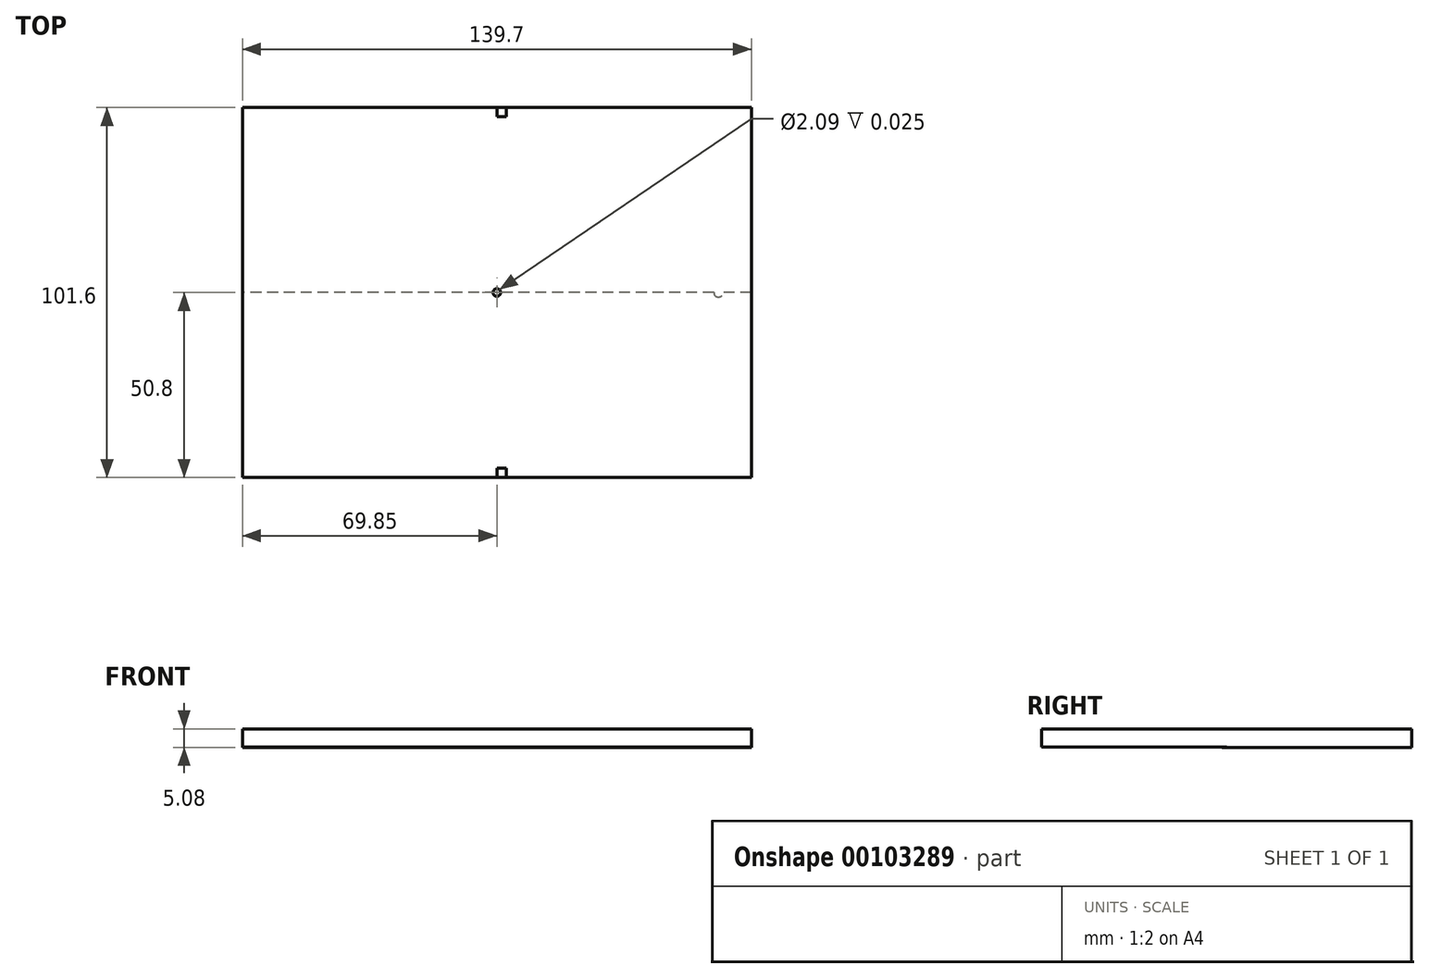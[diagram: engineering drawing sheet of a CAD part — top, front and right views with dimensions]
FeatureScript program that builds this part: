
annotation { "Feature Type Name" : "Feature", "Feature Type Description" : "" }
export const myFeature = defineFeature(function(context is Context, id is Id, definition is map)
    precondition{}
    {
        {
            var Q0;
            Q0=qCreatedBy(makeId("Top.planeOp"),FACE);
            var sketch = newSketch(context, id + "F0", { "sketchPlane" : qUnion([Q0])});
            skLineSegment(sketch, "E0.bottom", {"start": v(0, 0) * mm, "end": v(139.7, 0) * mm});
            skLineSegment(sketch, "E0.top", {"start": v(0, 101.6) * mm, "end": v(139.7, 101.6) * mm});
            skLineSegment(sketch, "E0.left", {"start": v(0, 0) * mm, "end": v(0, 101.6) * mm});
            skLineSegment(sketch, "E0.right", {"start": v(139.7, 0) * mm, "end": v(139.7, 101.6) * mm});
            skSolve(sketch);
        }
        {
            var Q0;
            Q0=makeQuery(id+"F0.imprint","IMPRINT",FACE,{"disambiguationData":[TD([[makeQuery(id+"F0.imprint","IMPRINT",EDGE,{"derivedFrom":sQuery(id+"F0.wireOp",EDGE,"E0.bottom")}),1.0]])]});
            extrude(context, id + "F1", {"entities" : qUnion([Q0]), "depth" : 5.08 * mm});
        }
        {
            var Q0;
            Q0=makeQuery(id+"F1.opExtrude","CAP_FACE",FACE,{"disambiguationData":[OSD([sQuery(id+"F0.wireOp",EDGE,"E0.bottom"),sQuery(id+"F0.wireOp",EDGE,"E0.top"),sQuery(id+"F0.wireOp",EDGE,"E0.left"),sQuery(id+"F0.wireOp",EDGE,"E0.right")])],"isStart":false});
            var sketch = newSketch(context, id + "F2", { "sketchPlane" : qUnion([Q0])});
            skLineSegment(sketch, "E1.bottom", {"start": v(69.85, 0) * mm, "end": v(72.4, 0) * mm});
            skLineSegment(sketch, "E1.top", {"start": v(69.85, 2.54) * mm, "end": v(72.4, 2.54) * mm});
            skLineSegment(sketch, "E1.left", {"start": v(69.85, 0) * mm, "end": v(69.85, 2.54) * mm});
            skLineSegment(sketch, "E1.right", {"start": v(72.4, 0) * mm, "end": v(72.4, 2.54) * mm});
            skLineSegment(sketch, "E2.bottom", {"start": v(69.85, 101.6) * mm, "end": v(72.39, 101.6) * mm});
            skLineSegment(sketch, "E2.top", {"start": v(69.85, 99.06) * mm, "end": v(72.39, 99.06) * mm});
            skLineSegment(sketch, "E2.left", {"start": v(69.85, 101.6) * mm, "end": v(69.85, 99.06) * mm});
            skLineSegment(sketch, "E2.right", {"start": v(72.39, 101.6) * mm, "end": v(72.39, 99.06) * mm});
            skCircle(sketch, "E3", {"center": v(69.85, 50.8) * mm, "radius": 1.05 * mm});
            skLineSegment(sketch, "E4", {"start": v(139.7, 50.8) * mm, "end": v(69.85, 50.8) * mm});
            skCircle(sketch, "E5", {"center": v(139.7, 50.8) * mm, "radius": 0.01 * mm});
            skSolve(sketch);
        }
        {
            var Q0;
            Q0=makeQuery(id+"F2.imprint","IMPRINT",FACE,{"disambiguationData":[TD([[makeQuery(id+"F2.imprint","IMPRINT",EDGE,{"derivedFrom":sQuery(id+"F2.wireOp",EDGE,"E1.bottom")}),1.0]])]});
            var Q1;
            Q1=makeQuery(id+"F2.imprint","IMPRINT",FACE,{"disambiguationData":[TD([[makeQuery(id+"F2.imprint","IMPRINT",EDGE,{"derivedFrom":sQuery(id+"F2.wireOp",EDGE,"E2.bottom")}),-1.0]])]});
            var Q2;
            Q2=makeQuery(id+"F2.imprint","IMPRINT",FACE,{"disambiguationData":[TD([[makeQuery(id+"F2.imprint","IMPRINT",EDGE,{"derivedFrom":sQuery(id+"F2.wireOp",EDGE,"E3")}),1.0]])]});
            extrude(context, id + "F3", {"entities" : qUnion([Q0, Q1, Q2]), "operationType" : NewBodyOperationType.REMOVE, "oppositeDirection" : true, "depth" : 0.03 * mm});
        }
        {
            var Q0;
            Q0=makeQuery(id+"F1.opExtrude","CAP_FACE",FACE,{"disambiguationData":[OSD([sQuery(id+"F0.wireOp",EDGE,"E0.bottom"),sQuery(id+"F0.wireOp",EDGE,"E0.top"),sQuery(id+"F0.wireOp",EDGE,"E0.left"),sQuery(id+"F0.wireOp",EDGE,"E0.right")])],"isStart":true});
            var sketch = newSketch(context, id + "F4", { "sketchPlane" : qUnion([Q0])});
            skLineSegment(sketch, "E6", {"start": v(139.7, -50.8) * mm, "end": v(0, -50.8) * mm});
            skCircle(sketch, "E7", {"center": v(130.68, -50.8) * mm, "radius": 1.27 * mm});
            skSolve(sketch);
        }
        {
            var Q0;
            {var subQ0=sQuery(id+"F4.wireOp",EDGE,"E7");var subQ1=sQuery(id+"F4.wireOp",EDGE,"E6");var subQ2=makeQuery(id+"F4.imprint","INTERSECT",VERTEX,{"disambiguationData":[OD(0.0)],"derivedFrom":[subQ1,subQ0]});Q0=makeQuery(id+"F4.imprint","IMPRINT",FACE,{"disambiguationData":[TD([[makeQuery(id+"F4.imprint","IMPRINT",EDGE,{"disambiguationData":[TD([[subQ2,-1.0]])],"derivedFrom":subQ1}),-1.0]])]});}
            extrude(context, id + "F5", {"entities" : qUnion([Q0]), "operationType" : NewBodyOperationType.REMOVE, "oppositeDirection" : true, "depth" : 0.03 * mm});
        }
    });
